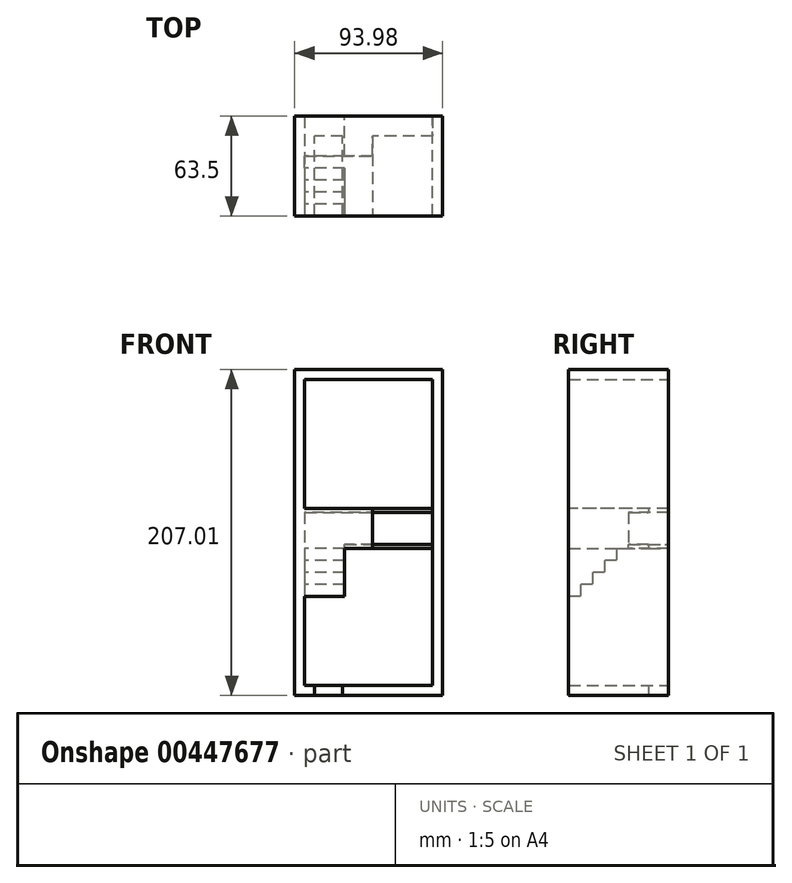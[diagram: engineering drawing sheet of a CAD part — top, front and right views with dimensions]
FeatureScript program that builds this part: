
annotation { "Feature Type Name" : "Feature", "Feature Type Description" : "" }
export const myFeature = defineFeature(function(context is Context, id is Id, definition is map)
    precondition{}
    {
        {
            var Q0;
            Q0=qCreatedBy(makeId("Front.planeOp"),FACE);
            var sketch = newSketch(context, id + "F0", { "sketchPlane" : qUnion([Q0])});
            skLineSegment(sketch, "E0.bottom", {"start": v(0, 194.31) * mm, "end": v(81.28, 194.31) * mm});
            skLineSegment(sketch, "E0.top", {"start": v(0, 0) * mm, "end": v(81.28, 0) * mm});
            skLineSegment(sketch, "E0.left", {"start": v(81.28, 194.3) * mm, "end": v(81.28, 89.66) * mm});
            skLineSegment(sketch, "E0.right", {"start": v(0, 194.31) * mm, "end": v(0, 89.66) * mm});
            skLineSegment(sketch, "E1.0", {"start": v(-6.35, -6.35) * mm, "end": v(87.63, -6.35) * mm});
            skLineSegment(sketch, "E1.1", {"start": v(-6.35, 200.66) * mm, "end": v(-6.35, -6.35) * mm});
            skLineSegment(sketch, "E1.2", {"start": v(-6.35, 200.66) * mm, "end": v(87.63, 200.66) * mm});
            skLineSegment(sketch, "E1.3", {"start": v(87.63, 200.66) * mm, "end": v(87.63, -6.35) * mm});
            skLineSegment(sketch, "E2", {"start": v(0, 89.66) * mm, "end": v(81.28, 89.66) * mm});
            skLineSegment(sketch, "E3", {"start": v(0, 87.12) * mm, "end": v(81.28, 87.12) * mm});
            skLineSegment(sketch, "E4", {"start": v(0, 87.12) * mm, "end": v(0, 0) * mm});
            skLineSegment(sketch, "E5", {"start": v(81.28, 87.12) * mm, "end": v(81.28, 0) * mm});
            skSolve(sketch);
        }
        {
            var Q0;
            Q0 = qSketchRegion(id + "F0", true);
            extrude(context, id + "F1", {"entities" : qUnion([Q0]), "depth" : 63.5 * mm});
        }
        {
            var Q0;
            Q0=makeQuery(id+"F1.opExtrude","SWEPT_FACE",FACE,{"disambiguationData":[OSD([sQuery(id+"F0.wireOp",EDGE,"E1.0")])]});
            var sketch = newSketch(context, id + "F2", { "sketchPlane" : qUnion([Q0])});
            skLineSegment(sketch, "E6.bottom", {"start": v(24.13, 63.5) * mm, "end": v(6.35, 63.5) * mm});
            skLineSegment(sketch, "E6.top", {"start": v(24.13, 12.7) * mm, "end": v(6.35, 12.7) * mm});
            skLineSegment(sketch, "E6.left", {"start": v(24.13, 63.5) * mm, "end": v(24.13, 12.7) * mm});
            skLineSegment(sketch, "E6.right", {"start": v(6.35, 63.5) * mm, "end": v(6.35, 12.7) * mm});
            skSolve(sketch);
        }
        {
            var Q0;
            Q0 = qSketchRegion(id + "F2", true);
            extrude(context, id + "F3", {"entities" : qUnion([Q0]), "operationType" : NewBodyOperationType.REMOVE, "endBound" : BoundingType.UP_TO_NEXT, "oppositeDirection" : true, "depth" : 25.4 * mm});
        }
        {
            var Q0;
            Q0=makeQuery(id+"F1.opExtrude","CAP_FACE",FACE,{"disambiguationData":[OSD([sQuery(id+"F0.wireOp",EDGE,"E0.bottom"),sQuery(id+"F0.wireOp",EDGE,"E0.top"),sQuery(id+"F0.wireOp",EDGE,"E0.left"),sQuery(id+"F0.wireOp",EDGE,"E0.right"),sQuery(id+"F0.wireOp",EDGE,"E1.0"),sQuery(id+"F0.wireOp",EDGE,"E1.1"),sQuery(id+"F0.wireOp",EDGE,"E1.2"),sQuery(id+"F0.wireOp",EDGE,"E1.3"),sQuery(id+"F0.wireOp",EDGE,"E2"),sQuery(id+"F0.wireOp",EDGE,"E3"),sQuery(id+"F0.wireOp",EDGE,"E4"),sQuery(id+"F0.wireOp",EDGE,"E5")])],"isStart":false});
            var sketch = newSketch(context, id + "F4", { "sketchPlane" : qUnion([Q0])});
            skLineSegment(sketch, "E7.bottom", {"start": v(0, 89.66) * mm, "end": v(25.4, 89.66) * mm});
            skLineSegment(sketch, "E7.top", {"start": v(0, 109.98) * mm, "end": v(25.4, 109.98) * mm});
            skLineSegment(sketch, "E7.left", {"start": v(0, 89.66) * mm, "end": v(0, 109.98) * mm});
            skLineSegment(sketch, "E7.right", {"start": v(25.4, 89.66) * mm, "end": v(25.4, 109.98) * mm});
            skSolve(sketch);
        }
        {
            var Q0;
            Q0 = qSketchRegion(id + "F4", true);
            extrude(context, id + "F5", {"entities" : qUnion([Q0]), "operationType" : NewBodyOperationType.ADD, "oppositeDirection" : true, "depth" : 38.1 * mm});
        }
        {
            var Q0;
            Q0=makeQuery(id+"F1.opExtrude","SWEPT_FACE",FACE,{"disambiguationData":[OSD([sQuery(id+"F0.wireOp",EDGE,"E2")])]});
            var sketch = newSketch(context, id + "F6", { "sketchPlane" : qUnion([Q0])});
            skLineSegment(sketch, "E8.bottom", {"start": v(25.4, -25.4) * mm, "end": v(0, -25.4) * mm});
            skLineSegment(sketch, "E8.top", {"start": v(25.4, 0) * mm, "end": v(0, 0) * mm});
            skLineSegment(sketch, "E8.left", {"start": v(25.4, -25.4) * mm, "end": v(25.4, 0) * mm});
            skLineSegment(sketch, "E8.right", {"start": v(0, -25.4) * mm, "end": v(0, 0) * mm});
            skSolve(sketch);
        }
        {
            var Q0;
            Q0 = qSketchRegion(id + "F6", true);
            extrude(context, id + "F7", {"entities" : qUnion([Q0]), "operationType" : NewBodyOperationType.REMOVE, "endBound" : BoundingType.UP_TO_NEXT, "oppositeDirection" : true, "depth" : 25.4 * mm});
        }
        {
            var Q0;
            Q0=makeQuery(id+"F7.boolean.opBoolean","MERGE",FACE,{"derivedFrom":[makeQuery(id+"F1.opExtrude","SWEPT_FACE",FACE,{"disambiguationData":[OSD([sQuery(id+"F0.wireOp",EDGE,"E4")])]}),makeQuery(id+"F1.opExtrude","SWEPT_FACE",FACE,{"disambiguationData":[OSD([sQuery(id+"F0.wireOp",EDGE,"E0.right")])]}),makeQuery(id+"F7.opExtrude","SWEPT_FACE",FACE,{"disambiguationData":[OSD([sQuery(id+"F6.wireOp",EDGE,"E8.right")])]})]});
            var sketch = newSketch(context, id + "F8", { "sketchPlane" : qUnion([Q0])});
            skLineSegment(sketch, "E9", {"start": v(-33.02, 87.12) * mm, "end": v(-33.02, 79.5) * mm});
            skLineSegment(sketch, "E10", {"start": v(-33.02, 79.5) * mm, "end": v(-40.64, 79.5) * mm});
            skLineSegment(sketch, "E11", {"start": v(-40.64, 79.5) * mm, "end": v(-40.64, 71.88) * mm});
            skLineSegment(sketch, "E12", {"start": v(-40.64, 71.88) * mm, "end": v(-48.26, 71.88) * mm});
            skLineSegment(sketch, "E13", {"start": v(-48.26, 71.88) * mm, "end": v(-48.26, 64.26) * mm});
            skLineSegment(sketch, "E14", {"start": v(-48.26, 64.26) * mm, "end": v(-55.88, 64.26) * mm});
            skLineSegment(sketch, "E15", {"start": v(-55.88, 64.26) * mm, "end": v(-55.88, 56.64) * mm});
            skLineSegment(sketch, "E16", {"start": v(-55.88, 56.64) * mm, "end": v(-63.5, 56.64) * mm});
            skLineSegment(sketch, "E17", {"start": v(-63.5, 56.64) * mm, "end": v(-63.5, 87.12) * mm});
            skLineSegment(sketch, "E18", {"start": v(-33.02, 87.12) * mm, "end": v(-63.5, 87.12) * mm});
            skLineSegment(sketch, "E19", {"start": v(-33.02, 87.12) * mm, "end": v(-25.4, 87.12) * mm, "construction": true});
            skSolve(sketch);
        }
        {
            var Q0;
            Q0 = qSketchRegion(id + "F8", true);
            var Q1;
            Q1=makeQuery(id+"F7.boolean.opBoolean","COPY",FACE,{"derivedFrom":makeQuery(id+"F7.opExtrude","SWEPT_FACE",FACE,{"disambiguationData":[OSD([sQuery(id+"F6.wireOp",EDGE,"E8.left")])]})});
            extrude(context, id + "F9", {"entities" : qUnion([Q0]), "operationType" : NewBodyOperationType.ADD, "endBound" : BoundingType.UP_TO_SURFACE, "endBoundEntityFace" : qUnion([Q1]), "depth" : 25.4 * mm});
        }
        {
            var Q0;
            Q0=makeQuery(id+"F9.boolean.opBoolean","MERGE",FACE,{"derivedFrom":[makeQuery(id+"F5.boolean.opBoolean","MERGE",FACE,{"derivedFrom":[makeQuery(id+"F1.opExtrude","CAP_FACE",FACE,{"disambiguationData":[OSD([sQuery(id+"F0.wireOp",EDGE,"E0.bottom"),sQuery(id+"F0.wireOp",EDGE,"E0.top"),sQuery(id+"F0.wireOp",EDGE,"E0.left"),sQuery(id+"F0.wireOp",EDGE,"E0.right"),sQuery(id+"F0.wireOp",EDGE,"E1.0"),sQuery(id+"F0.wireOp",EDGE,"E1.1"),sQuery(id+"F0.wireOp",EDGE,"E1.2"),sQuery(id+"F0.wireOp",EDGE,"E1.3"),sQuery(id+"F0.wireOp",EDGE,"E2"),sQuery(id+"F0.wireOp",EDGE,"E3"),sQuery(id+"F0.wireOp",EDGE,"E4"),sQuery(id+"F0.wireOp",EDGE,"E5")])],"isStart":false}),makeQuery(id+"F5.opExtrude","CAP_FACE",FACE,{"disambiguationData":[OSD([sQuery(id+"F4.wireOp",EDGE,"E7.bottom"),sQuery(id+"F4.wireOp",EDGE,"E7.top"),sQuery(id+"F4.wireOp",EDGE,"E7.left"),sQuery(id+"F4.wireOp",EDGE,"E7.right")])],"isStart":true})]}),makeQuery(id+"F9.opExtrude","SWEPT_FACE",FACE,{"disambiguationData":[OSD([sQuery(id+"F8.wireOp",EDGE,"E17")])]})]});
            var sketch = newSketch(context, id + "F10", { "sketchPlane" : qUnion([Q0])});
            skLineSegment(sketch, "E20", {"start": v(0, 109.98) * mm, "end": v(0, 112.52) * mm});
            skLineSegment(sketch, "E21", {"start": v(0, 112.52) * mm, "end": v(81.28, 112.52) * mm});
            skLineSegment(sketch, "E22", {"start": v(81.28, 112.52) * mm, "end": v(81.28, 109.98) * mm});
            skLineSegment(sketch, "E23", {"start": v(81.28, 109.98) * mm, "end": v(0, 109.98) * mm});
            skSolve(sketch);
        }
        {
            var Q0;
            Q0 = qSketchRegion(id + "F10", true);
            var Q1;
            Q1=makeQuery(id+"F1.opExtrude","CAP_FACE",FACE,{"disambiguationData":[OSD([sQuery(id+"F0.wireOp",EDGE,"E0.bottom"),sQuery(id+"F0.wireOp",EDGE,"E0.top"),sQuery(id+"F0.wireOp",EDGE,"E0.left"),sQuery(id+"F0.wireOp",EDGE,"E0.right"),sQuery(id+"F0.wireOp",EDGE,"E1.0"),sQuery(id+"F0.wireOp",EDGE,"E1.1"),sQuery(id+"F0.wireOp",EDGE,"E1.2"),sQuery(id+"F0.wireOp",EDGE,"E1.3"),sQuery(id+"F0.wireOp",EDGE,"E2"),sQuery(id+"F0.wireOp",EDGE,"E3"),sQuery(id+"F0.wireOp",EDGE,"E4"),sQuery(id+"F0.wireOp",EDGE,"E5")])],"isStart":true});
            extrude(context, id + "F11", {"entities" : qUnion([Q0]), "operationType" : NewBodyOperationType.ADD, "endBound" : BoundingType.UP_TO_SURFACE, "oppositeDirection" : true, "endBoundEntityFace" : qUnion([Q1]), "depth" : 25.4 * mm});
        }
        {
            var Q0;
            Q0=makeQuery(id+"F1.opExtrude","SWEPT_FACE",FACE,{"disambiguationData":[OSD([sQuery(id+"F0.wireOp",EDGE,"E3")])]});
            var sketch = newSketch(context, id + "F12", { "sketchPlane" : qUnion([Q0])});
            skLineSegment(sketch, "E24.bottom", {"start": v(81.28, 63.5) * mm, "end": v(43.18, 63.5) * mm});
            skLineSegment(sketch, "E24.top", {"start": v(81.28, 12.7) * mm, "end": v(43.18, 12.7) * mm});
            skLineSegment(sketch, "E24.left", {"start": v(81.28, 63.5) * mm, "end": v(81.28, 12.7) * mm});
            skLineSegment(sketch, "E24.right", {"start": v(43.18, 63.5) * mm, "end": v(43.18, 12.7) * mm});
            skSolve(sketch);
        }
        {
            var Q0;
            Q0 = qSketchRegion(id + "F12", true);
            var Q1;
            Q1=makeQuery(id+"F11.opExtrude","SWEPT_FACE",FACE,{"disambiguationData":[OSD([sQuery(id+"F10.wireOp",EDGE,"E21")])]});
            extrude(context, id + "F13", {"entities" : qUnion([Q0]), "operationType" : NewBodyOperationType.REMOVE, "endBound" : BoundingType.UP_TO_SURFACE, "oppositeDirection" : true, "endBoundEntityFace" : qUnion([Q1]), "depth" : 25.4 * mm});
        }
        {
            var Q0;
            Q0=makeQuery(id+"F11.boolean.opBoolean","MERGE",FACE,{"derivedFrom":[makeQuery(id+"F9.boolean.opBoolean","MERGE",FACE,{"derivedFrom":[makeQuery(id+"F5.boolean.opBoolean","MERGE",FACE,{"derivedFrom":[makeQuery(id+"F1.opExtrude","CAP_FACE",FACE,{"disambiguationData":[OSD([sQuery(id+"F0.wireOp",EDGE,"E0.bottom"),sQuery(id+"F0.wireOp",EDGE,"E0.top"),sQuery(id+"F0.wireOp",EDGE,"E0.left"),sQuery(id+"F0.wireOp",EDGE,"E0.right"),sQuery(id+"F0.wireOp",EDGE,"E1.0"),sQuery(id+"F0.wireOp",EDGE,"E1.1"),sQuery(id+"F0.wireOp",EDGE,"E1.2"),sQuery(id+"F0.wireOp",EDGE,"E1.3"),sQuery(id+"F0.wireOp",EDGE,"E2"),sQuery(id+"F0.wireOp",EDGE,"E3"),sQuery(id+"F0.wireOp",EDGE,"E4"),sQuery(id+"F0.wireOp",EDGE,"E5")])],"isStart":false}),makeQuery(id+"F5.opExtrude","CAP_FACE",FACE,{"disambiguationData":[OSD([sQuery(id+"F4.wireOp",EDGE,"E7.bottom"),sQuery(id+"F4.wireOp",EDGE,"E7.top"),sQuery(id+"F4.wireOp",EDGE,"E7.left"),sQuery(id+"F4.wireOp",EDGE,"E7.right")])],"isStart":true})]}),makeQuery(id+"F9.opExtrude","SWEPT_FACE",FACE,{"disambiguationData":[OSD([sQuery(id+"F8.wireOp",EDGE,"E17")])]})]}),makeQuery(id+"F11.opExtrude","CAP_FACE",FACE,{"disambiguationData":[OSD([sQuery(id+"F10.wireOp",EDGE,"E20"),sQuery(id+"F10.wireOp",EDGE,"E21"),sQuery(id+"F10.wireOp",EDGE,"E22"),sQuery(id+"F10.wireOp",EDGE,"E23")])],"isStart":true})]});
            var sketch = newSketch(context, id + "F14", { "sketchPlane" : qUnion([Q0])});
            skLineSegment(sketch, "E25.bottom", {"start": v(25.4, 89.66) * mm, "end": v(43.18, 89.66) * mm});
            skLineSegment(sketch, "E25.top", {"start": v(25.4, 109.98) * mm, "end": v(43.18, 109.98) * mm});
            skLineSegment(sketch, "E25.left", {"start": v(25.4, 89.66) * mm, "end": v(25.4, 109.98) * mm});
            skLineSegment(sketch, "E25.right", {"start": v(43.18, 89.66) * mm, "end": v(43.18, 109.98) * mm});
            skSolve(sketch);
        }
        {
            var Q0;
            Q0 = qSketchRegion(id + "F14", true);
            var Q1;
            Q1=makeQuery(id+"F7.boolean.opBoolean","MERGE",FACE,{"derivedFrom":[makeQuery(id+"F5.opExtrude","CAP_FACE",FACE,{"disambiguationData":[OSD([sQuery(id+"F4.wireOp",EDGE,"E7.bottom"),sQuery(id+"F4.wireOp",EDGE,"E7.top"),sQuery(id+"F4.wireOp",EDGE,"E7.left"),sQuery(id+"F4.wireOp",EDGE,"E7.right")])],"isStart":false}),makeQuery(id+"F7.opExtrude","SWEPT_FACE",FACE,{"disambiguationData":[OSD([sQuery(id+"F6.wireOp",EDGE,"E8.bottom")])]})]});
            extrude(context, id + "F15", {"entities" : qUnion([Q0]), "operationType" : NewBodyOperationType.ADD, "endBound" : BoundingType.UP_TO_SURFACE, "oppositeDirection" : true, "endBoundEntityFace" : qUnion([Q1]), "depth" : 25.4 * mm});
        }
    });
